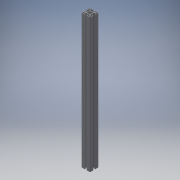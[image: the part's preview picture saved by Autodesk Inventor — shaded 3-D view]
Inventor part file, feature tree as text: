
AUTODESK INVENTOR PART (.ipt)
format: ipt  version: 2018 (Build 220112000, 112)  size: 587,776 bytes
history: native  units: mm
features: other x1, extrude x1, sketch x1
ambient origin geometry x8: Origin, YZ Plane, XZ Plane, XY Plane, X Axis, Y Axis, Z Axis, Center Point
bodies: Body1 (feature_tree)
feature tree (3):
  other  "Sólido1"
  extrude  "Extrusão1"  [1 undecoded]
  sketch  "Esboço1"  dims[d0=640.0mm d1=0.0mm]
note: 1 required parameter value undecoded (feature->parameter linkage not recoverable at this tier; creation-order binding heuristic only, values carry confidence <= 0.55)
